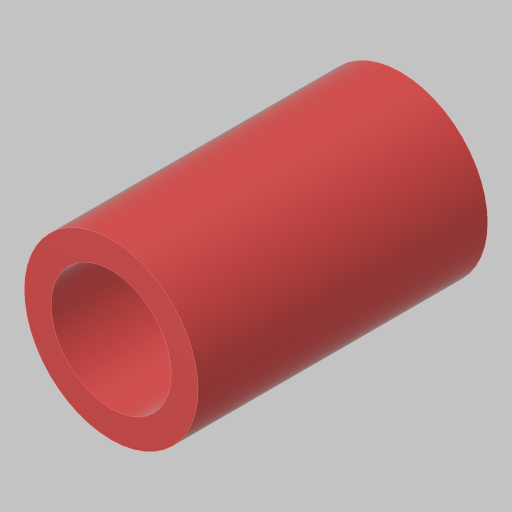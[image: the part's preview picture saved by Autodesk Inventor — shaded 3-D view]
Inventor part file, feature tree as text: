
AUTODESK INVENTOR PART (.ipt)
format: ipt  version: 2023.5 (Build 275446000, 446)  size: 116,736 bytes
history: native  units: in
note: dims shown in document units (in); Inventor stores cm internally (conversion verified against a paired STEP export)
features: extrude x1, sketch x1
ambient origin geometry x8: Origin, YZ Plane, XZ Plane, XY Plane, X Axis, Y Axis, Z Axis, Center Point
bodies: Solid1 (feature_tree)
feature tree (2):
  extrude  "Extrusion1"  Depth=1.35in
  sketch  "Sketch1"  dims[d0=0.56in d1=0.125in d2=1.35in d3=0.0in]
